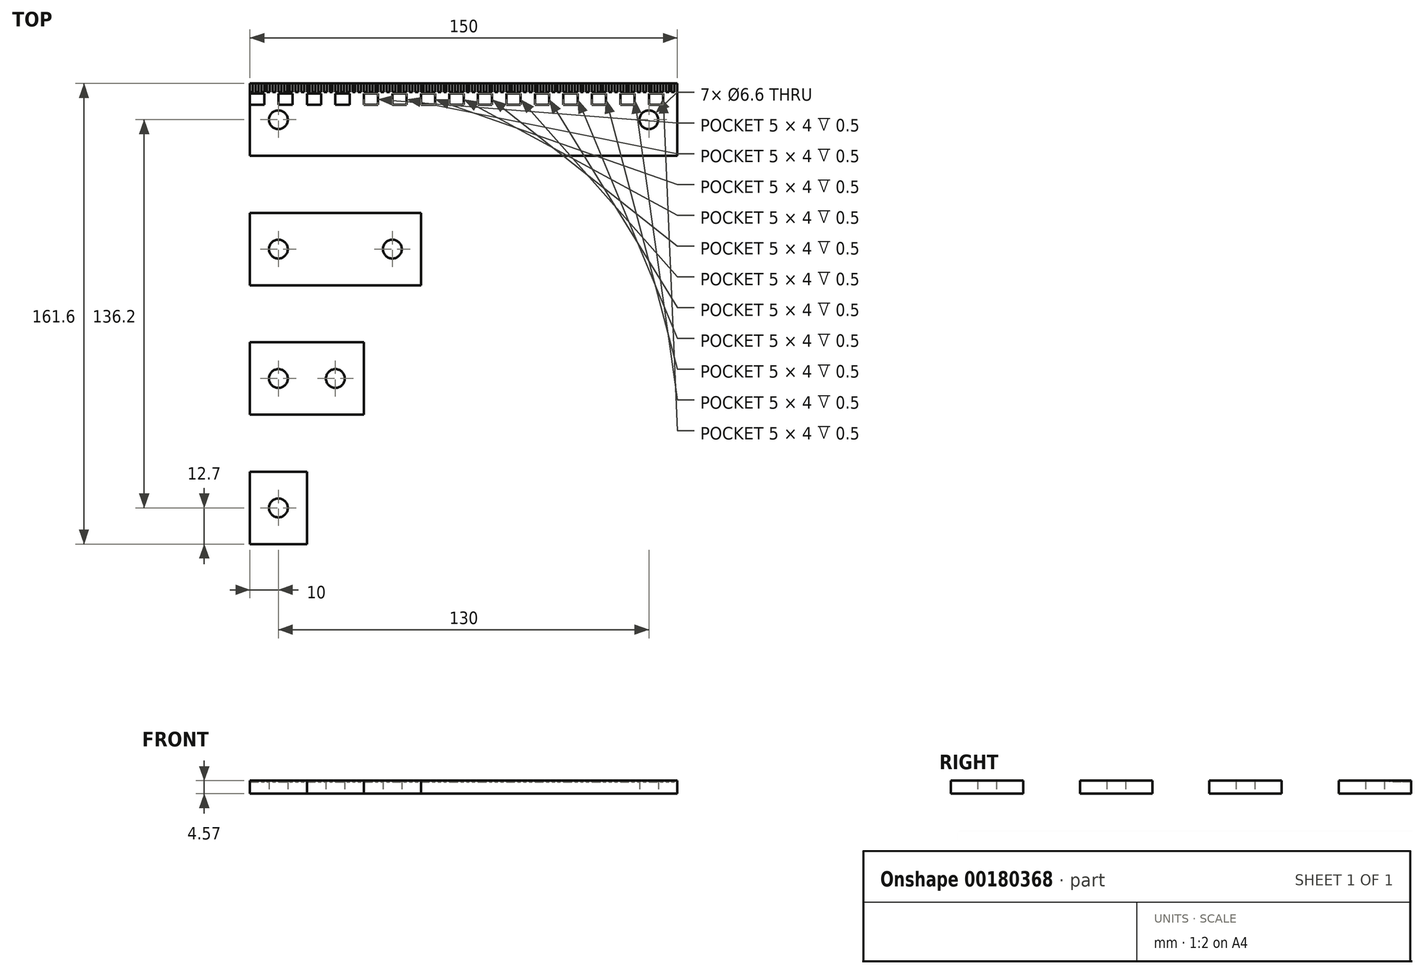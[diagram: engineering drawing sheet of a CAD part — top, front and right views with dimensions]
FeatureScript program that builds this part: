
annotation { "Feature Type Name" : "Feature", "Feature Type Description" : "" }
export const myFeature = defineFeature(function(context is Context, id is Id, definition is map)
    precondition{}
    {
        {
            var Q0;
            Q0=qCreatedBy(makeId("Top.planeOp"),FACE);
            var sketch = newSketch(context, id + "F0", { "sketchPlane" : qUnion([Q0])});
            skLineSegment(sketch, "E0.bottom", {"start": v(0, 161.6) * mm, "end": v(150, 161.6) * mm});
            skLineSegment(sketch, "E0.top", {"start": v(0, 136.2) * mm, "end": v(150, 136.2) * mm});
            skLineSegment(sketch, "E0.left", {"start": v(0, 161.6) * mm, "end": v(0, 136.2) * mm});
            skLineSegment(sketch, "E0.right", {"start": v(150, 161.6) * mm, "end": v(150, 136.2) * mm});
            skLineSegment(sketch, "E1.bottom", {"start": v(0, 116.2) * mm, "end": v(60, 116.2) * mm});
            skLineSegment(sketch, "E1.top", {"start": v(0, 90.8) * mm, "end": v(60, 90.8) * mm});
            skLineSegment(sketch, "E1.left", {"start": v(0, 116.2) * mm, "end": v(0, 90.8) * mm});
            skLineSegment(sketch, "E1.right", {"start": v(60, 116.2) * mm, "end": v(60, 90.8) * mm});
            skLineSegment(sketch, "E2.bottom", {"start": v(0, 70.8) * mm, "end": v(40, 70.8) * mm});
            skLineSegment(sketch, "E2.top", {"start": v(0, 45.4) * mm, "end": v(40, 45.4) * mm});
            skLineSegment(sketch, "E2.left", {"start": v(0, 70.8) * mm, "end": v(0, 45.4) * mm});
            skLineSegment(sketch, "E2.right", {"start": v(40, 70.8) * mm, "end": v(40, 45.4) * mm});
            skLineSegment(sketch, "E3.bottom", {"start": v(0, 25.4) * mm, "end": v(20, 25.4) * mm});
            skLineSegment(sketch, "E3.top", {"start": v(0, 0) * mm, "end": v(20, 0) * mm});
            skLineSegment(sketch, "E3.left", {"start": v(0, 25.4) * mm, "end": v(0, 0) * mm});
            skLineSegment(sketch, "E3.right", {"start": v(20, 25.4) * mm, "end": v(20, 0) * mm});
            skLineSegment(sketch, "E4", {"start": v(0, 136.2) * mm, "end": v(0, 116.2) * mm, "construction": true});
            skLineSegment(sketch, "E5", {"start": v(0, 90.8) * mm, "end": v(0, 70.8) * mm, "construction": true});
            skLineSegment(sketch, "E6", {"start": v(0, 45.4) * mm, "end": v(0, 25.4) * mm, "construction": true});
            skLineSegment(sketch, "E7", {"start": v(0, 12.7) * mm, "end": v(20, 12.7) * mm, "construction": true});
            skLineSegment(sketch, "E8", {"start": v(0, 58.1) * mm, "end": v(40, 58.1) * mm, "construction": true});
            skLineSegment(sketch, "E9", {"start": v(0, 103.5) * mm, "end": v(60, 103.5) * mm, "construction": true});
            skLineSegment(sketch, "E10", {"start": v(0, 148.9) * mm, "end": v(150, 148.9) * mm, "construction": true});
            skCircle(sketch, "E11", {"center": v(10, 12.7) * mm, "radius": 3.3 * mm});
            skCircle(sketch, "E12", {"center": v(30, 58.1) * mm, "radius": 3.3 * mm});
            skCircle(sketch, "E13", {"center": v(10, 58.1) * mm, "radius": 3.3 * mm});
            skCircle(sketch, "E14", {"center": v(50, 103.5) * mm, "radius": 3.3 * mm});
            skCircle(sketch, "E15", {"center": v(10, 103.5) * mm, "radius": 3.3 * mm});
            skCircle(sketch, "E16", {"center": v(140, 148.9) * mm, "radius": 3.3 * mm});
            skCircle(sketch, "E17", {"center": v(10, 148.9) * mm, "radius": 3.3 * mm});
            skLineSegment(sketch, "E18", {"start": v(10, 148.9) * mm, "end": v(10, 103.5) * mm, "construction": true});
            skLineSegment(sketch, "E19", {"start": v(10, 58.1) * mm, "end": v(10, 103.5) * mm, "construction": true});
            skSolve(sketch);
        }
        {
            var Q0;
            Q0 = qSketchRegion(id + "F0", true);
            extrude(context, id + "F1", {"entities" : qUnion([Q0]), "depth" : 4.57 * mm});
        }
        {
            var Q0;
            Q0=makeQuery(id+"F1.opExtrude","CAP_FACE",FACE,{"disambiguationData":[OSD([sQuery(id+"F0.wireOp",EDGE,"E0.bottom"),sQuery(id+"F0.wireOp",EDGE,"E0.top"),sQuery(id+"F0.wireOp",EDGE,"E0.left"),sQuery(id+"F0.wireOp",EDGE,"E0.right"),sQuery(id+"F0.wireOp",EDGE,"E16"),sQuery(id+"F0.wireOp",EDGE,"E17")])],"isStart":false});
            var sketch = newSketch(context, id + "F2", { "sketchPlane" : qUnion([Q0])});
            skLineSegment(sketch, "E20.bottom", {"start": v(0, 161.6) * mm, "end": v(1, 161.6) * mm});
            skLineSegment(sketch, "E20.top", {"start": v(0, 158.6) * mm, "end": v(1, 158.6) * mm});
            skLineSegment(sketch, "E20.left", {"start": v(0, 161.6) * mm, "end": v(0, 158.6) * mm});
            skLineSegment(sketch, "E20.right", {"start": v(1, 161.6) * mm, "end": v(1, 158.6) * mm});
            skLineSegment(sketch, "E21.1.0.0", {"start": v(3, 161.6) * mm, "end": v(3, 158.6) * mm});
            skLineSegment(sketch, "E21.1.0.1", {"start": v(2, 161.6) * mm, "end": v(2, 158.6) * mm});
            skLineSegment(sketch, "E21.1.0.2", {"start": v(2, 158.6) * mm, "end": v(3, 158.6) * mm});
            skLineSegment(sketch, "E21.1.0.3", {"start": v(2, 161.6) * mm, "end": v(3, 161.6) * mm});
            skLineSegment(sketch, "E21.2.0.0", {"start": v(5, 161.6) * mm, "end": v(5, 158.6) * mm});
            skLineSegment(sketch, "E21.2.0.1", {"start": v(4, 161.6) * mm, "end": v(4, 158.6) * mm});
            skLineSegment(sketch, "E21.2.0.2", {"start": v(4, 158.6) * mm, "end": v(5, 158.6) * mm});
            skLineSegment(sketch, "E21.2.0.3", {"start": v(4, 161.6) * mm, "end": v(5, 161.6) * mm});
            skLineSegment(sketch, "E21.3.0.0", {"start": v(7, 161.6) * mm, "end": v(7, 158.6) * mm});
            skLineSegment(sketch, "E21.3.0.1", {"start": v(6, 161.6) * mm, "end": v(6, 158.6) * mm});
            skLineSegment(sketch, "E21.3.0.2", {"start": v(6, 158.6) * mm, "end": v(7, 158.6) * mm});
            skLineSegment(sketch, "E21.3.0.3", {"start": v(6, 161.6) * mm, "end": v(7, 161.6) * mm});
            skLineSegment(sketch, "E21.4.0.0", {"start": v(9, 161.6) * mm, "end": v(9, 158.6) * mm});
            skLineSegment(sketch, "E21.4.0.1", {"start": v(8, 161.6) * mm, "end": v(8, 158.6) * mm});
            skLineSegment(sketch, "E21.4.0.2", {"start": v(8, 158.6) * mm, "end": v(9, 158.6) * mm});
            skLineSegment(sketch, "E21.4.0.3", {"start": v(8, 161.6) * mm, "end": v(9, 161.6) * mm});
            skLineSegment(sketch, "E21.5.0.0", {"start": v(11, 161.6) * mm, "end": v(11, 158.6) * mm});
            skLineSegment(sketch, "E21.5.0.1", {"start": v(10, 161.6) * mm, "end": v(10, 158.6) * mm});
            skLineSegment(sketch, "E21.5.0.2", {"start": v(10, 158.6) * mm, "end": v(11, 158.6) * mm});
            skLineSegment(sketch, "E21.5.0.3", {"start": v(10, 161.6) * mm, "end": v(11, 161.6) * mm});
            skLineSegment(sketch, "E21.6.0.0", {"start": v(13, 161.6) * mm, "end": v(13, 158.6) * mm});
            skLineSegment(sketch, "E21.6.0.1", {"start": v(12, 161.6) * mm, "end": v(12, 158.6) * mm});
            skLineSegment(sketch, "E21.6.0.2", {"start": v(12, 158.6) * mm, "end": v(13, 158.6) * mm});
            skLineSegment(sketch, "E21.6.0.3", {"start": v(12, 161.6) * mm, "end": v(13, 161.6) * mm});
            skLineSegment(sketch, "E21.7.0.0", {"start": v(15, 161.6) * mm, "end": v(15, 158.6) * mm});
            skLineSegment(sketch, "E21.7.0.1", {"start": v(14, 161.6) * mm, "end": v(14, 158.6) * mm});
            skLineSegment(sketch, "E21.7.0.2", {"start": v(14, 158.6) * mm, "end": v(15, 158.6) * mm});
            skLineSegment(sketch, "E21.7.0.3", {"start": v(14, 161.6) * mm, "end": v(15, 161.6) * mm});
            skLineSegment(sketch, "E21.8.0.0", {"start": v(17, 161.6) * mm, "end": v(17, 158.6) * mm});
            skLineSegment(sketch, "E21.8.0.1", {"start": v(16, 161.6) * mm, "end": v(16, 158.6) * mm});
            skLineSegment(sketch, "E21.8.0.2", {"start": v(16, 158.6) * mm, "end": v(17, 158.6) * mm});
            skLineSegment(sketch, "E21.8.0.3", {"start": v(16, 161.6) * mm, "end": v(17, 161.6) * mm});
            skLineSegment(sketch, "E21.9.0.0", {"start": v(19, 161.6) * mm, "end": v(19, 158.6) * mm});
            skLineSegment(sketch, "E21.9.0.1", {"start": v(18, 161.6) * mm, "end": v(18, 158.6) * mm});
            skLineSegment(sketch, "E21.9.0.2", {"start": v(18, 158.6) * mm, "end": v(19, 158.6) * mm});
            skLineSegment(sketch, "E21.9.0.3", {"start": v(18, 161.6) * mm, "end": v(19, 161.6) * mm});
            skLineSegment(sketch, "E21.10.0.0", {"start": v(21, 161.6) * mm, "end": v(21, 158.6) * mm});
            skLineSegment(sketch, "E21.10.0.1", {"start": v(20, 161.6) * mm, "end": v(20, 158.6) * mm});
            skLineSegment(sketch, "E21.10.0.2", {"start": v(20, 158.6) * mm, "end": v(21, 158.6) * mm});
            skLineSegment(sketch, "E21.10.0.3", {"start": v(20, 161.6) * mm, "end": v(21, 161.6) * mm});
            skLineSegment(sketch, "E21.11.0.0", {"start": v(23, 161.6) * mm, "end": v(23, 158.6) * mm});
            skLineSegment(sketch, "E21.11.0.1", {"start": v(22, 161.6) * mm, "end": v(22, 158.6) * mm});
            skLineSegment(sketch, "E21.11.0.2", {"start": v(22, 158.6) * mm, "end": v(23, 158.6) * mm});
            skLineSegment(sketch, "E21.11.0.3", {"start": v(22, 161.6) * mm, "end": v(23, 161.6) * mm});
            skLineSegment(sketch, "E21.12.0.0", {"start": v(25, 161.6) * mm, "end": v(25, 158.6) * mm});
            skLineSegment(sketch, "E21.12.0.1", {"start": v(24, 161.6) * mm, "end": v(24, 158.6) * mm});
            skLineSegment(sketch, "E21.12.0.2", {"start": v(24, 158.6) * mm, "end": v(25, 158.6) * mm});
            skLineSegment(sketch, "E21.12.0.3", {"start": v(24, 161.6) * mm, "end": v(25, 161.6) * mm});
            skLineSegment(sketch, "E21.13.0.0", {"start": v(27, 161.6) * mm, "end": v(27, 158.6) * mm});
            skLineSegment(sketch, "E21.13.0.1", {"start": v(26, 161.6) * mm, "end": v(26, 158.6) * mm});
            skLineSegment(sketch, "E21.13.0.2", {"start": v(26, 158.6) * mm, "end": v(27, 158.6) * mm});
            skLineSegment(sketch, "E21.13.0.3", {"start": v(26, 161.6) * mm, "end": v(27, 161.6) * mm});
            skLineSegment(sketch, "E21.14.0.0", {"start": v(29, 161.6) * mm, "end": v(29, 158.6) * mm});
            skLineSegment(sketch, "E21.14.0.1", {"start": v(28, 161.6) * mm, "end": v(28, 158.6) * mm});
            skLineSegment(sketch, "E21.14.0.2", {"start": v(28, 158.6) * mm, "end": v(29, 158.6) * mm});
            skLineSegment(sketch, "E21.14.0.3", {"start": v(28, 161.6) * mm, "end": v(29, 161.6) * mm});
            skLineSegment(sketch, "E21.15.0.0", {"start": v(31, 161.6) * mm, "end": v(31, 158.6) * mm});
            skLineSegment(sketch, "E21.15.0.1", {"start": v(30, 161.6) * mm, "end": v(30, 158.6) * mm});
            skLineSegment(sketch, "E21.15.0.2", {"start": v(30, 158.6) * mm, "end": v(31, 158.6) * mm});
            skLineSegment(sketch, "E21.15.0.3", {"start": v(30, 161.6) * mm, "end": v(31, 161.6) * mm});
            skLineSegment(sketch, "E21.16.0.0", {"start": v(33, 161.6) * mm, "end": v(33, 158.6) * mm});
            skLineSegment(sketch, "E21.16.0.1", {"start": v(32, 161.6) * mm, "end": v(32, 158.6) * mm});
            skLineSegment(sketch, "E21.16.0.2", {"start": v(32, 158.6) * mm, "end": v(33, 158.6) * mm});
            skLineSegment(sketch, "E21.16.0.3", {"start": v(32, 161.6) * mm, "end": v(33, 161.6) * mm});
            skLineSegment(sketch, "E21.17.0.0", {"start": v(35, 161.6) * mm, "end": v(35, 158.6) * mm});
            skLineSegment(sketch, "E21.17.0.1", {"start": v(34, 161.6) * mm, "end": v(34, 158.6) * mm});
            skLineSegment(sketch, "E21.17.0.2", {"start": v(34, 158.6) * mm, "end": v(35, 158.6) * mm});
            skLineSegment(sketch, "E21.17.0.3", {"start": v(34, 161.6) * mm, "end": v(35, 161.6) * mm});
            skLineSegment(sketch, "E21.18.0.0", {"start": v(37, 161.6) * mm, "end": v(37, 158.6) * mm});
            skLineSegment(sketch, "E21.18.0.1", {"start": v(36, 161.6) * mm, "end": v(36, 158.6) * mm});
            skLineSegment(sketch, "E21.18.0.2", {"start": v(36, 158.6) * mm, "end": v(37, 158.6) * mm});
            skLineSegment(sketch, "E21.18.0.3", {"start": v(36, 161.6) * mm, "end": v(37, 161.6) * mm});
            skLineSegment(sketch, "E21.19.0.0", {"start": v(39, 161.6) * mm, "end": v(39, 158.6) * mm});
            skLineSegment(sketch, "E21.19.0.1", {"start": v(38, 161.6) * mm, "end": v(38, 158.6) * mm});
            skLineSegment(sketch, "E21.19.0.2", {"start": v(38, 158.6) * mm, "end": v(39, 158.6) * mm});
            skLineSegment(sketch, "E21.19.0.3", {"start": v(38, 161.6) * mm, "end": v(39, 161.6) * mm});
            skLineSegment(sketch, "E21.20.0.0", {"start": v(41, 161.6) * mm, "end": v(41, 158.6) * mm});
            skLineSegment(sketch, "E21.20.0.1", {"start": v(40, 161.6) * mm, "end": v(40, 158.6) * mm});
            skLineSegment(sketch, "E21.20.0.2", {"start": v(40, 158.6) * mm, "end": v(41, 158.6) * mm});
            skLineSegment(sketch, "E21.20.0.3", {"start": v(40, 161.6) * mm, "end": v(41, 161.6) * mm});
            skLineSegment(sketch, "E21.21.0.0", {"start": v(43, 161.6) * mm, "end": v(43, 158.6) * mm});
            skLineSegment(sketch, "E21.21.0.1", {"start": v(42, 161.6) * mm, "end": v(42, 158.6) * mm});
            skLineSegment(sketch, "E21.21.0.2", {"start": v(42, 158.6) * mm, "end": v(43, 158.6) * mm});
            skLineSegment(sketch, "E21.21.0.3", {"start": v(42, 161.6) * mm, "end": v(43, 161.6) * mm});
            skLineSegment(sketch, "E21.22.0.0", {"start": v(45, 161.6) * mm, "end": v(45, 158.6) * mm});
            skLineSegment(sketch, "E21.22.0.1", {"start": v(44, 161.6) * mm, "end": v(44, 158.6) * mm});
            skLineSegment(sketch, "E21.22.0.2", {"start": v(44, 158.6) * mm, "end": v(45, 158.6) * mm});
            skLineSegment(sketch, "E21.22.0.3", {"start": v(44, 161.6) * mm, "end": v(45, 161.6) * mm});
            skLineSegment(sketch, "E21.23.0.0", {"start": v(47, 161.6) * mm, "end": v(47, 158.6) * mm});
            skLineSegment(sketch, "E21.23.0.1", {"start": v(46, 161.6) * mm, "end": v(46, 158.6) * mm});
            skLineSegment(sketch, "E21.23.0.2", {"start": v(46, 158.6) * mm, "end": v(47, 158.6) * mm});
            skLineSegment(sketch, "E21.23.0.3", {"start": v(46, 161.6) * mm, "end": v(47, 161.6) * mm});
            skLineSegment(sketch, "E21.24.0.0", {"start": v(49, 161.6) * mm, "end": v(49, 158.6) * mm});
            skLineSegment(sketch, "E21.24.0.1", {"start": v(48, 161.6) * mm, "end": v(48, 158.6) * mm});
            skLineSegment(sketch, "E21.24.0.2", {"start": v(48, 158.6) * mm, "end": v(49, 158.6) * mm});
            skLineSegment(sketch, "E21.24.0.3", {"start": v(48, 161.6) * mm, "end": v(49, 161.6) * mm});
            skLineSegment(sketch, "E21.25.0.0", {"start": v(51, 161.6) * mm, "end": v(51, 158.6) * mm});
            skLineSegment(sketch, "E21.25.0.1", {"start": v(50, 161.6) * mm, "end": v(50, 158.6) * mm});
            skLineSegment(sketch, "E21.25.0.2", {"start": v(50, 158.6) * mm, "end": v(51, 158.6) * mm});
            skLineSegment(sketch, "E21.25.0.3", {"start": v(50, 161.6) * mm, "end": v(51, 161.6) * mm});
            skLineSegment(sketch, "E21.26.0.0", {"start": v(53, 161.6) * mm, "end": v(53, 158.6) * mm});
            skLineSegment(sketch, "E21.26.0.1", {"start": v(52, 161.6) * mm, "end": v(52, 158.6) * mm});
            skLineSegment(sketch, "E21.26.0.2", {"start": v(52, 158.6) * mm, "end": v(53, 158.6) * mm});
            skLineSegment(sketch, "E21.26.0.3", {"start": v(52, 161.6) * mm, "end": v(53, 161.6) * mm});
            skLineSegment(sketch, "E21.27.0.0", {"start": v(55, 161.6) * mm, "end": v(55, 158.6) * mm});
            skLineSegment(sketch, "E21.27.0.1", {"start": v(54, 161.6) * mm, "end": v(54, 158.6) * mm});
            skLineSegment(sketch, "E21.27.0.2", {"start": v(54, 158.6) * mm, "end": v(55, 158.6) * mm});
            skLineSegment(sketch, "E21.27.0.3", {"start": v(54, 161.6) * mm, "end": v(55, 161.6) * mm});
            skLineSegment(sketch, "E21.28.0.0", {"start": v(57, 161.6) * mm, "end": v(57, 158.6) * mm});
            skLineSegment(sketch, "E21.28.0.1", {"start": v(56, 161.6) * mm, "end": v(56, 158.6) * mm});
            skLineSegment(sketch, "E21.28.0.2", {"start": v(56, 158.6) * mm, "end": v(57, 158.6) * mm});
            skLineSegment(sketch, "E21.28.0.3", {"start": v(56, 161.6) * mm, "end": v(57, 161.6) * mm});
            skLineSegment(sketch, "E21.29.0.0", {"start": v(59, 161.6) * mm, "end": v(59, 158.6) * mm});
            skLineSegment(sketch, "E21.29.0.1", {"start": v(58, 161.6) * mm, "end": v(58, 158.6) * mm});
            skLineSegment(sketch, "E21.29.0.2", {"start": v(58, 158.6) * mm, "end": v(59, 158.6) * mm});
            skLineSegment(sketch, "E21.29.0.3", {"start": v(58, 161.6) * mm, "end": v(59, 161.6) * mm});
            skLineSegment(sketch, "E21.30.0.0", {"start": v(61, 161.6) * mm, "end": v(61, 158.6) * mm});
            skLineSegment(sketch, "E21.30.0.1", {"start": v(60, 161.6) * mm, "end": v(60, 158.6) * mm});
            skLineSegment(sketch, "E21.30.0.2", {"start": v(60, 158.6) * mm, "end": v(61, 158.6) * mm});
            skLineSegment(sketch, "E21.30.0.3", {"start": v(60, 161.6) * mm, "end": v(61, 161.6) * mm});
            skLineSegment(sketch, "E21.31.0.0", {"start": v(63, 161.6) * mm, "end": v(63, 158.6) * mm});
            skLineSegment(sketch, "E21.31.0.1", {"start": v(62, 161.6) * mm, "end": v(62, 158.6) * mm});
            skLineSegment(sketch, "E21.31.0.2", {"start": v(62, 158.6) * mm, "end": v(63, 158.6) * mm});
            skLineSegment(sketch, "E21.31.0.3", {"start": v(62, 161.6) * mm, "end": v(63, 161.6) * mm});
            skLineSegment(sketch, "E21.32.0.0", {"start": v(65, 161.6) * mm, "end": v(65, 158.6) * mm});
            skLineSegment(sketch, "E21.32.0.1", {"start": v(64, 161.6) * mm, "end": v(64, 158.6) * mm});
            skLineSegment(sketch, "E21.32.0.2", {"start": v(64, 158.6) * mm, "end": v(65, 158.6) * mm});
            skLineSegment(sketch, "E21.32.0.3", {"start": v(64, 161.6) * mm, "end": v(65, 161.6) * mm});
            skLineSegment(sketch, "E21.33.0.0", {"start": v(67, 161.6) * mm, "end": v(67, 158.6) * mm});
            skLineSegment(sketch, "E21.33.0.1", {"start": v(66, 161.6) * mm, "end": v(66, 158.6) * mm});
            skLineSegment(sketch, "E21.33.0.2", {"start": v(66, 158.6) * mm, "end": v(67, 158.6) * mm});
            skLineSegment(sketch, "E21.33.0.3", {"start": v(66, 161.6) * mm, "end": v(67, 161.6) * mm});
            skLineSegment(sketch, "E21.34.0.0", {"start": v(69, 161.6) * mm, "end": v(69, 158.6) * mm});
            skLineSegment(sketch, "E21.34.0.1", {"start": v(68, 161.6) * mm, "end": v(68, 158.6) * mm});
            skLineSegment(sketch, "E21.34.0.2", {"start": v(68, 158.6) * mm, "end": v(69, 158.6) * mm});
            skLineSegment(sketch, "E21.34.0.3", {"start": v(68, 161.6) * mm, "end": v(69, 161.6) * mm});
            skLineSegment(sketch, "E21.35.0.0", {"start": v(71, 161.6) * mm, "end": v(71, 158.6) * mm});
            skLineSegment(sketch, "E21.35.0.1", {"start": v(70, 161.6) * mm, "end": v(70, 158.6) * mm});
            skLineSegment(sketch, "E21.35.0.2", {"start": v(70, 158.6) * mm, "end": v(71, 158.6) * mm});
            skLineSegment(sketch, "E21.35.0.3", {"start": v(70, 161.6) * mm, "end": v(71, 161.6) * mm});
            skLineSegment(sketch, "E21.36.0.0", {"start": v(73, 161.6) * mm, "end": v(73, 158.6) * mm});
            skLineSegment(sketch, "E21.36.0.1", {"start": v(72, 161.6) * mm, "end": v(72, 158.6) * mm});
            skLineSegment(sketch, "E21.36.0.2", {"start": v(72, 158.6) * mm, "end": v(73, 158.6) * mm});
            skLineSegment(sketch, "E21.36.0.3", {"start": v(72, 161.6) * mm, "end": v(73, 161.6) * mm});
            skLineSegment(sketch, "E21.37.0.0", {"start": v(75, 161.6) * mm, "end": v(75, 158.6) * mm});
            skLineSegment(sketch, "E21.37.0.1", {"start": v(74, 161.6) * mm, "end": v(74, 158.6) * mm});
            skLineSegment(sketch, "E21.37.0.2", {"start": v(74, 158.6) * mm, "end": v(75, 158.6) * mm});
            skLineSegment(sketch, "E21.37.0.3", {"start": v(74, 161.6) * mm, "end": v(75, 161.6) * mm});
            skLineSegment(sketch, "E21.38.0.0", {"start": v(77, 161.6) * mm, "end": v(77, 158.6) * mm});
            skLineSegment(sketch, "E21.38.0.1", {"start": v(76, 161.6) * mm, "end": v(76, 158.6) * mm});
            skLineSegment(sketch, "E21.38.0.2", {"start": v(76, 158.6) * mm, "end": v(77, 158.6) * mm});
            skLineSegment(sketch, "E21.38.0.3", {"start": v(76, 161.6) * mm, "end": v(77, 161.6) * mm});
            skLineSegment(sketch, "E21.39.0.0", {"start": v(79, 161.6) * mm, "end": v(79, 158.6) * mm});
            skLineSegment(sketch, "E21.39.0.1", {"start": v(78, 161.6) * mm, "end": v(78, 158.6) * mm});
            skLineSegment(sketch, "E21.39.0.2", {"start": v(78, 158.6) * mm, "end": v(79, 158.6) * mm});
            skLineSegment(sketch, "E21.39.0.3", {"start": v(78, 161.6) * mm, "end": v(79, 161.6) * mm});
            skLineSegment(sketch, "E21.40.0.0", {"start": v(81, 161.6) * mm, "end": v(81, 158.6) * mm});
            skLineSegment(sketch, "E21.40.0.1", {"start": v(80, 161.6) * mm, "end": v(80, 158.6) * mm});
            skLineSegment(sketch, "E21.40.0.2", {"start": v(80, 158.6) * mm, "end": v(81, 158.6) * mm});
            skLineSegment(sketch, "E21.40.0.3", {"start": v(80, 161.6) * mm, "end": v(81, 161.6) * mm});
            skLineSegment(sketch, "E21.41.0.0", {"start": v(83, 161.6) * mm, "end": v(83, 158.6) * mm});
            skLineSegment(sketch, "E21.41.0.1", {"start": v(82, 161.6) * mm, "end": v(82, 158.6) * mm});
            skLineSegment(sketch, "E21.41.0.2", {"start": v(82, 158.6) * mm, "end": v(83, 158.6) * mm});
            skLineSegment(sketch, "E21.41.0.3", {"start": v(82, 161.6) * mm, "end": v(83, 161.6) * mm});
            skLineSegment(sketch, "E21.42.0.0", {"start": v(85, 161.6) * mm, "end": v(85, 158.6) * mm});
            skLineSegment(sketch, "E21.42.0.1", {"start": v(84, 161.6) * mm, "end": v(84, 158.6) * mm});
            skLineSegment(sketch, "E21.42.0.2", {"start": v(84, 158.6) * mm, "end": v(85, 158.6) * mm});
            skLineSegment(sketch, "E21.42.0.3", {"start": v(84, 161.6) * mm, "end": v(85, 161.6) * mm});
            skLineSegment(sketch, "E21.43.0.0", {"start": v(87, 161.6) * mm, "end": v(87, 158.6) * mm});
            skLineSegment(sketch, "E21.43.0.1", {"start": v(86, 161.6) * mm, "end": v(86, 158.6) * mm});
            skLineSegment(sketch, "E21.43.0.2", {"start": v(86, 158.6) * mm, "end": v(87, 158.6) * mm});
            skLineSegment(sketch, "E21.43.0.3", {"start": v(86, 161.6) * mm, "end": v(87, 161.6) * mm});
            skLineSegment(sketch, "E21.44.0.0", {"start": v(89, 161.6) * mm, "end": v(89, 158.6) * mm});
            skLineSegment(sketch, "E21.44.0.1", {"start": v(88, 161.6) * mm, "end": v(88, 158.6) * mm});
            skLineSegment(sketch, "E21.44.0.2", {"start": v(88, 158.6) * mm, "end": v(89, 158.6) * mm});
            skLineSegment(sketch, "E21.44.0.3", {"start": v(88, 161.6) * mm, "end": v(89, 161.6) * mm});
            skLineSegment(sketch, "E21.45.0.0", {"start": v(91, 161.6) * mm, "end": v(91, 158.6) * mm});
            skLineSegment(sketch, "E21.45.0.1", {"start": v(90, 161.6) * mm, "end": v(90, 158.6) * mm});
            skLineSegment(sketch, "E21.45.0.2", {"start": v(90, 158.6) * mm, "end": v(91, 158.6) * mm});
            skLineSegment(sketch, "E21.45.0.3", {"start": v(90, 161.6) * mm, "end": v(91, 161.6) * mm});
            skLineSegment(sketch, "E21.46.0.0", {"start": v(93, 161.6) * mm, "end": v(93, 158.6) * mm});
            skLineSegment(sketch, "E21.46.0.1", {"start": v(92, 161.6) * mm, "end": v(92, 158.6) * mm});
            skLineSegment(sketch, "E21.46.0.2", {"start": v(92, 158.6) * mm, "end": v(93, 158.6) * mm});
            skLineSegment(sketch, "E21.46.0.3", {"start": v(92, 161.6) * mm, "end": v(93, 161.6) * mm});
            skLineSegment(sketch, "E21.47.0.0", {"start": v(95, 161.6) * mm, "end": v(95, 158.6) * mm});
            skLineSegment(sketch, "E21.47.0.1", {"start": v(94, 161.6) * mm, "end": v(94, 158.6) * mm});
            skLineSegment(sketch, "E21.47.0.2", {"start": v(94, 158.6) * mm, "end": v(95, 158.6) * mm});
            skLineSegment(sketch, "E21.47.0.3", {"start": v(94, 161.6) * mm, "end": v(95, 161.6) * mm});
            skLineSegment(sketch, "E21.48.0.0", {"start": v(97, 161.6) * mm, "end": v(97, 158.6) * mm});
            skLineSegment(sketch, "E21.48.0.1", {"start": v(96, 161.6) * mm, "end": v(96, 158.6) * mm});
            skLineSegment(sketch, "E21.48.0.2", {"start": v(96, 158.6) * mm, "end": v(97, 158.6) * mm});
            skLineSegment(sketch, "E21.48.0.3", {"start": v(96, 161.6) * mm, "end": v(97, 161.6) * mm});
            skLineSegment(sketch, "E21.49.0.0", {"start": v(99, 161.6) * mm, "end": v(99, 158.6) * mm});
            skLineSegment(sketch, "E21.49.0.1", {"start": v(98, 161.6) * mm, "end": v(98, 158.6) * mm});
            skLineSegment(sketch, "E21.49.0.2", {"start": v(98, 158.6) * mm, "end": v(99, 158.6) * mm});
            skLineSegment(sketch, "E21.49.0.3", {"start": v(98, 161.6) * mm, "end": v(99, 161.6) * mm});
            skLineSegment(sketch, "E21.50.0.0", {"start": v(101, 161.6) * mm, "end": v(101, 158.6) * mm});
            skLineSegment(sketch, "E21.50.0.1", {"start": v(100, 161.6) * mm, "end": v(100, 158.6) * mm});
            skLineSegment(sketch, "E21.50.0.2", {"start": v(100, 158.6) * mm, "end": v(101, 158.6) * mm});
            skLineSegment(sketch, "E21.50.0.3", {"start": v(100, 161.6) * mm, "end": v(101, 161.6) * mm});
            skLineSegment(sketch, "E21.51.0.0", {"start": v(103, 161.6) * mm, "end": v(103, 158.6) * mm});
            skLineSegment(sketch, "E21.51.0.1", {"start": v(102, 161.6) * mm, "end": v(102, 158.6) * mm});
            skLineSegment(sketch, "E21.51.0.2", {"start": v(102, 158.6) * mm, "end": v(103, 158.6) * mm});
            skLineSegment(sketch, "E21.51.0.3", {"start": v(102, 161.6) * mm, "end": v(103, 161.6) * mm});
            skLineSegment(sketch, "E21.52.0.0", {"start": v(105, 161.6) * mm, "end": v(105, 158.6) * mm});
            skLineSegment(sketch, "E21.52.0.1", {"start": v(104, 161.6) * mm, "end": v(104, 158.6) * mm});
            skLineSegment(sketch, "E21.52.0.2", {"start": v(104, 158.6) * mm, "end": v(105, 158.6) * mm});
            skLineSegment(sketch, "E21.52.0.3", {"start": v(104, 161.6) * mm, "end": v(105, 161.6) * mm});
            skLineSegment(sketch, "E21.53.0.0", {"start": v(107, 161.6) * mm, "end": v(107, 158.6) * mm});
            skLineSegment(sketch, "E21.53.0.1", {"start": v(106, 161.6) * mm, "end": v(106, 158.6) * mm});
            skLineSegment(sketch, "E21.53.0.2", {"start": v(106, 158.6) * mm, "end": v(107, 158.6) * mm});
            skLineSegment(sketch, "E21.53.0.3", {"start": v(106, 161.6) * mm, "end": v(107, 161.6) * mm});
            skLineSegment(sketch, "E21.54.0.0", {"start": v(109, 161.6) * mm, "end": v(109, 158.6) * mm});
            skLineSegment(sketch, "E21.54.0.1", {"start": v(108, 161.6) * mm, "end": v(108, 158.6) * mm});
            skLineSegment(sketch, "E21.54.0.2", {"start": v(108, 158.6) * mm, "end": v(109, 158.6) * mm});
            skLineSegment(sketch, "E21.54.0.3", {"start": v(108, 161.6) * mm, "end": v(109, 161.6) * mm});
            skLineSegment(sketch, "E21.55.0.0", {"start": v(111, 161.6) * mm, "end": v(111, 158.6) * mm});
            skLineSegment(sketch, "E21.55.0.1", {"start": v(110, 161.6) * mm, "end": v(110, 158.6) * mm});
            skLineSegment(sketch, "E21.55.0.2", {"start": v(110, 158.6) * mm, "end": v(111, 158.6) * mm});
            skLineSegment(sketch, "E21.55.0.3", {"start": v(110, 161.6) * mm, "end": v(111, 161.6) * mm});
            skLineSegment(sketch, "E21.56.0.0", {"start": v(113, 161.6) * mm, "end": v(113, 158.6) * mm});
            skLineSegment(sketch, "E21.56.0.1", {"start": v(112, 161.6) * mm, "end": v(112, 158.6) * mm});
            skLineSegment(sketch, "E21.56.0.2", {"start": v(112, 158.6) * mm, "end": v(113, 158.6) * mm});
            skLineSegment(sketch, "E21.56.0.3", {"start": v(112, 161.6) * mm, "end": v(113, 161.6) * mm});
            skLineSegment(sketch, "E21.57.0.0", {"start": v(115, 161.6) * mm, "end": v(115, 158.6) * mm});
            skLineSegment(sketch, "E21.57.0.1", {"start": v(114, 161.6) * mm, "end": v(114, 158.6) * mm});
            skLineSegment(sketch, "E21.57.0.2", {"start": v(114, 158.6) * mm, "end": v(115, 158.6) * mm});
            skLineSegment(sketch, "E21.57.0.3", {"start": v(114, 161.6) * mm, "end": v(115, 161.6) * mm});
            skLineSegment(sketch, "E21.58.0.0", {"start": v(117, 161.6) * mm, "end": v(117, 158.6) * mm});
            skLineSegment(sketch, "E21.58.0.1", {"start": v(116, 161.6) * mm, "end": v(116, 158.6) * mm});
            skLineSegment(sketch, "E21.58.0.2", {"start": v(116, 158.6) * mm, "end": v(117, 158.6) * mm});
            skLineSegment(sketch, "E21.58.0.3", {"start": v(116, 161.6) * mm, "end": v(117, 161.6) * mm});
            skLineSegment(sketch, "E21.59.0.0", {"start": v(119, 161.6) * mm, "end": v(119, 158.6) * mm});
            skLineSegment(sketch, "E21.59.0.1", {"start": v(118, 161.6) * mm, "end": v(118, 158.6) * mm});
            skLineSegment(sketch, "E21.59.0.2", {"start": v(118, 158.6) * mm, "end": v(119, 158.6) * mm});
            skLineSegment(sketch, "E21.59.0.3", {"start": v(118, 161.6) * mm, "end": v(119, 161.6) * mm});
            skLineSegment(sketch, "E21.60.0.0", {"start": v(121, 161.6) * mm, "end": v(121, 158.6) * mm});
            skLineSegment(sketch, "E21.60.0.1", {"start": v(120, 161.6) * mm, "end": v(120, 158.6) * mm});
            skLineSegment(sketch, "E21.60.0.2", {"start": v(120, 158.6) * mm, "end": v(121, 158.6) * mm});
            skLineSegment(sketch, "E21.60.0.3", {"start": v(120, 161.6) * mm, "end": v(121, 161.6) * mm});
            skLineSegment(sketch, "E21.61.0.0", {"start": v(123, 161.6) * mm, "end": v(123, 158.6) * mm});
            skLineSegment(sketch, "E21.61.0.1", {"start": v(122, 161.6) * mm, "end": v(122, 158.6) * mm});
            skLineSegment(sketch, "E21.61.0.2", {"start": v(122, 158.6) * mm, "end": v(123, 158.6) * mm});
            skLineSegment(sketch, "E21.61.0.3", {"start": v(122, 161.6) * mm, "end": v(123, 161.6) * mm});
            skLineSegment(sketch, "E21.62.0.0", {"start": v(125, 161.6) * mm, "end": v(125, 158.6) * mm});
            skLineSegment(sketch, "E21.62.0.1", {"start": v(124, 161.6) * mm, "end": v(124, 158.6) * mm});
            skLineSegment(sketch, "E21.62.0.2", {"start": v(124, 158.6) * mm, "end": v(125, 158.6) * mm});
            skLineSegment(sketch, "E21.62.0.3", {"start": v(124, 161.6) * mm, "end": v(125, 161.6) * mm});
            skLineSegment(sketch, "E21.63.0.0", {"start": v(127, 161.6) * mm, "end": v(127, 158.6) * mm});
            skLineSegment(sketch, "E21.63.0.1", {"start": v(126, 161.6) * mm, "end": v(126, 158.6) * mm});
            skLineSegment(sketch, "E21.63.0.2", {"start": v(126, 158.6) * mm, "end": v(127, 158.6) * mm});
            skLineSegment(sketch, "E21.63.0.3", {"start": v(126, 161.6) * mm, "end": v(127, 161.6) * mm});
            skLineSegment(sketch, "E21.64.0.0", {"start": v(129, 161.6) * mm, "end": v(129, 158.6) * mm});
            skLineSegment(sketch, "E21.64.0.1", {"start": v(128, 161.6) * mm, "end": v(128, 158.6) * mm});
            skLineSegment(sketch, "E21.64.0.2", {"start": v(128, 158.6) * mm, "end": v(129, 158.6) * mm});
            skLineSegment(sketch, "E21.64.0.3", {"start": v(128, 161.6) * mm, "end": v(129, 161.6) * mm});
            skLineSegment(sketch, "E21.65.0.0", {"start": v(131, 161.6) * mm, "end": v(131, 158.6) * mm});
            skLineSegment(sketch, "E21.65.0.1", {"start": v(130, 161.6) * mm, "end": v(130, 158.6) * mm});
            skLineSegment(sketch, "E21.65.0.2", {"start": v(130, 158.6) * mm, "end": v(131, 158.6) * mm});
            skLineSegment(sketch, "E21.65.0.3", {"start": v(130, 161.6) * mm, "end": v(131, 161.6) * mm});
            skLineSegment(sketch, "E21.66.0.0", {"start": v(133, 161.6) * mm, "end": v(133, 158.6) * mm});
            skLineSegment(sketch, "E21.66.0.1", {"start": v(132, 161.6) * mm, "end": v(132, 158.6) * mm});
            skLineSegment(sketch, "E21.66.0.2", {"start": v(132, 158.6) * mm, "end": v(133, 158.6) * mm});
            skLineSegment(sketch, "E21.66.0.3", {"start": v(132, 161.6) * mm, "end": v(133, 161.6) * mm});
            skLineSegment(sketch, "E21.67.0.0", {"start": v(135, 161.6) * mm, "end": v(135, 158.6) * mm});
            skLineSegment(sketch, "E21.67.0.1", {"start": v(134, 161.6) * mm, "end": v(134, 158.6) * mm});
            skLineSegment(sketch, "E21.67.0.2", {"start": v(134, 158.6) * mm, "end": v(135, 158.6) * mm});
            skLineSegment(sketch, "E21.67.0.3", {"start": v(134, 161.6) * mm, "end": v(135, 161.6) * mm});
            skLineSegment(sketch, "E21.68.0.0", {"start": v(137, 161.6) * mm, "end": v(137, 158.6) * mm});
            skLineSegment(sketch, "E21.68.0.1", {"start": v(136, 161.6) * mm, "end": v(136, 158.6) * mm});
            skLineSegment(sketch, "E21.68.0.2", {"start": v(136, 158.6) * mm, "end": v(137, 158.6) * mm});
            skLineSegment(sketch, "E21.68.0.3", {"start": v(136, 161.6) * mm, "end": v(137, 161.6) * mm});
            skLineSegment(sketch, "E21.69.0.0", {"start": v(139, 161.6) * mm, "end": v(139, 158.6) * mm});
            skLineSegment(sketch, "E21.69.0.1", {"start": v(138, 161.6) * mm, "end": v(138, 158.6) * mm});
            skLineSegment(sketch, "E21.69.0.2", {"start": v(138, 158.6) * mm, "end": v(139, 158.6) * mm});
            skLineSegment(sketch, "E21.69.0.3", {"start": v(138, 161.6) * mm, "end": v(139, 161.6) * mm});
            skLineSegment(sketch, "E21.70.0.0", {"start": v(141, 161.6) * mm, "end": v(141, 158.6) * mm});
            skLineSegment(sketch, "E21.70.0.1", {"start": v(140, 161.6) * mm, "end": v(140, 158.6) * mm});
            skLineSegment(sketch, "E21.70.0.2", {"start": v(140, 158.6) * mm, "end": v(141, 158.6) * mm});
            skLineSegment(sketch, "E21.70.0.3", {"start": v(140, 161.6) * mm, "end": v(141, 161.6) * mm});
            skLineSegment(sketch, "E21.71.0.0", {"start": v(143, 161.6) * mm, "end": v(143, 158.6) * mm});
            skLineSegment(sketch, "E21.71.0.1", {"start": v(142, 161.6) * mm, "end": v(142, 158.6) * mm});
            skLineSegment(sketch, "E21.71.0.2", {"start": v(142, 158.6) * mm, "end": v(143, 158.6) * mm});
            skLineSegment(sketch, "E21.71.0.3", {"start": v(142, 161.6) * mm, "end": v(143, 161.6) * mm});
            skLineSegment(sketch, "E21.72.0.0", {"start": v(145, 161.6) * mm, "end": v(145, 158.6) * mm});
            skLineSegment(sketch, "E21.72.0.1", {"start": v(144, 161.6) * mm, "end": v(144, 158.6) * mm});
            skLineSegment(sketch, "E21.72.0.2", {"start": v(144, 158.6) * mm, "end": v(145, 158.6) * mm});
            skLineSegment(sketch, "E21.72.0.3", {"start": v(144, 161.6) * mm, "end": v(145, 161.6) * mm});
            skLineSegment(sketch, "E21.73.0.0", {"start": v(147, 161.6) * mm, "end": v(147, 158.6) * mm});
            skLineSegment(sketch, "E21.73.0.1", {"start": v(146, 161.6) * mm, "end": v(146, 158.6) * mm});
            skLineSegment(sketch, "E21.73.0.2", {"start": v(146, 158.6) * mm, "end": v(147, 158.6) * mm});
            skLineSegment(sketch, "E21.73.0.3", {"start": v(146, 161.6) * mm, "end": v(147, 161.6) * mm});
            skLineSegment(sketch, "E21.74.0.0", {"start": v(149, 161.6) * mm, "end": v(149, 158.6) * mm});
            skLineSegment(sketch, "E21.74.0.1", {"start": v(148, 161.6) * mm, "end": v(148, 158.6) * mm});
            skLineSegment(sketch, "E21.74.0.2", {"start": v(148, 158.6) * mm, "end": v(149, 158.6) * mm});
            skLineSegment(sketch, "E21.74.0.3", {"start": v(148, 161.6) * mm, "end": v(149, 161.6) * mm});
            skLineSegment(sketch, "E21.direction1", {"start": v(0, 158.6) * mm, "end": v(2, 158.6) * mm, "construction": true});
            skLineSegment(sketch, "E22.bottom", {"start": v(0, 158.1) * mm, "end": v(5, 158.1) * mm});
            skLineSegment(sketch, "E22.top", {"start": v(0, 154.1) * mm, "end": v(5, 154.1) * mm});
            skLineSegment(sketch, "E22.left", {"start": v(0, 158.1) * mm, "end": v(0, 154.1) * mm});
            skLineSegment(sketch, "E22.right", {"start": v(5, 158.1) * mm, "end": v(5, 154.1) * mm});
            skLineSegment(sketch, "E23.1.0.0", {"start": v(15, 158.1) * mm, "end": v(15, 154.1) * mm});
            skLineSegment(sketch, "E23.1.0.1", {"start": v(10, 158.1) * mm, "end": v(15, 158.1) * mm});
            skLineSegment(sketch, "E23.1.0.2", {"start": v(10, 158.1) * mm, "end": v(10, 154.1) * mm});
            skLineSegment(sketch, "E23.1.0.3", {"start": v(10, 154.1) * mm, "end": v(15, 154.1) * mm});
            skLineSegment(sketch, "E23.2.0.0", {"start": v(25, 158.1) * mm, "end": v(25, 154.1) * mm});
            skLineSegment(sketch, "E23.2.0.1", {"start": v(20, 158.1) * mm, "end": v(25, 158.1) * mm});
            skLineSegment(sketch, "E23.2.0.2", {"start": v(20, 158.1) * mm, "end": v(20, 154.1) * mm});
            skLineSegment(sketch, "E23.2.0.3", {"start": v(20, 154.1) * mm, "end": v(25, 154.1) * mm});
            skLineSegment(sketch, "E23.3.0.0", {"start": v(35, 158.1) * mm, "end": v(35, 154.1) * mm});
            skLineSegment(sketch, "E23.3.0.1", {"start": v(30, 158.1) * mm, "end": v(35, 158.1) * mm});
            skLineSegment(sketch, "E23.3.0.2", {"start": v(30, 158.1) * mm, "end": v(30, 154.1) * mm});
            skLineSegment(sketch, "E23.3.0.3", {"start": v(30, 154.1) * mm, "end": v(35, 154.1) * mm});
            skLineSegment(sketch, "E23.4.0.0", {"start": v(45, 158.1) * mm, "end": v(45, 154.1) * mm});
            skLineSegment(sketch, "E23.4.0.1", {"start": v(40, 158.1) * mm, "end": v(45, 158.1) * mm});
            skLineSegment(sketch, "E23.4.0.2", {"start": v(40, 158.1) * mm, "end": v(40, 154.1) * mm});
            skLineSegment(sketch, "E23.4.0.3", {"start": v(40, 154.1) * mm, "end": v(45, 154.1) * mm});
            skLineSegment(sketch, "E23.5.0.0", {"start": v(55, 158.1) * mm, "end": v(55, 154.1) * mm});
            skLineSegment(sketch, "E23.5.0.1", {"start": v(50, 158.1) * mm, "end": v(55, 158.1) * mm});
            skLineSegment(sketch, "E23.5.0.2", {"start": v(50, 158.1) * mm, "end": v(50, 154.1) * mm});
            skLineSegment(sketch, "E23.5.0.3", {"start": v(50, 154.1) * mm, "end": v(55, 154.1) * mm});
            skLineSegment(sketch, "E23.6.0.0", {"start": v(65, 158.1) * mm, "end": v(65, 154.1) * mm});
            skLineSegment(sketch, "E23.6.0.1", {"start": v(60, 158.1) * mm, "end": v(65, 158.1) * mm});
            skLineSegment(sketch, "E23.6.0.2", {"start": v(60, 158.1) * mm, "end": v(60, 154.1) * mm});
            skLineSegment(sketch, "E23.6.0.3", {"start": v(60, 154.1) * mm, "end": v(65, 154.1) * mm});
            skLineSegment(sketch, "E23.7.0.0", {"start": v(75, 158.1) * mm, "end": v(75, 154.1) * mm});
            skLineSegment(sketch, "E23.7.0.1", {"start": v(70, 158.1) * mm, "end": v(75, 158.1) * mm});
            skLineSegment(sketch, "E23.7.0.2", {"start": v(70, 158.1) * mm, "end": v(70, 154.1) * mm});
            skLineSegment(sketch, "E23.7.0.3", {"start": v(70, 154.1) * mm, "end": v(75, 154.1) * mm});
            skLineSegment(sketch, "E23.8.0.0", {"start": v(85, 158.1) * mm, "end": v(85, 154.1) * mm});
            skLineSegment(sketch, "E23.8.0.1", {"start": v(80, 158.1) * mm, "end": v(85, 158.1) * mm});
            skLineSegment(sketch, "E23.8.0.2", {"start": v(80, 158.1) * mm, "end": v(80, 154.1) * mm});
            skLineSegment(sketch, "E23.8.0.3", {"start": v(80, 154.1) * mm, "end": v(85, 154.1) * mm});
            skLineSegment(sketch, "E23.9.0.0", {"start": v(95, 158.1) * mm, "end": v(95, 154.1) * mm});
            skLineSegment(sketch, "E23.9.0.1", {"start": v(90, 158.1) * mm, "end": v(95, 158.1) * mm});
            skLineSegment(sketch, "E23.9.0.2", {"start": v(90, 158.1) * mm, "end": v(90, 154.1) * mm});
            skLineSegment(sketch, "E23.9.0.3", {"start": v(90, 154.1) * mm, "end": v(95, 154.1) * mm});
            skLineSegment(sketch, "E23.10.0.0", {"start": v(105, 158.1) * mm, "end": v(105, 154.1) * mm});
            skLineSegment(sketch, "E23.10.0.1", {"start": v(100, 158.1) * mm, "end": v(105, 158.1) * mm});
            skLineSegment(sketch, "E23.10.0.2", {"start": v(100, 158.1) * mm, "end": v(100, 154.1) * mm});
            skLineSegment(sketch, "E23.10.0.3", {"start": v(100, 154.1) * mm, "end": v(105, 154.1) * mm});
            skLineSegment(sketch, "E23.11.0.0", {"start": v(115, 158.1) * mm, "end": v(115, 154.1) * mm});
            skLineSegment(sketch, "E23.11.0.1", {"start": v(110, 158.1) * mm, "end": v(115, 158.1) * mm});
            skLineSegment(sketch, "E23.11.0.2", {"start": v(110, 158.1) * mm, "end": v(110, 154.1) * mm});
            skLineSegment(sketch, "E23.11.0.3", {"start": v(110, 154.1) * mm, "end": v(115, 154.1) * mm});
            skLineSegment(sketch, "E23.12.0.0", {"start": v(125, 158.1) * mm, "end": v(125, 154.1) * mm});
            skLineSegment(sketch, "E23.12.0.1", {"start": v(120, 158.1) * mm, "end": v(125, 158.1) * mm});
            skLineSegment(sketch, "E23.12.0.2", {"start": v(120, 158.1) * mm, "end": v(120, 154.1) * mm});
            skLineSegment(sketch, "E23.12.0.3", {"start": v(120, 154.1) * mm, "end": v(125, 154.1) * mm});
            skLineSegment(sketch, "E23.13.0.0", {"start": v(135, 158.1) * mm, "end": v(135, 154.1) * mm});
            skLineSegment(sketch, "E23.13.0.1", {"start": v(130, 158.1) * mm, "end": v(135, 158.1) * mm});
            skLineSegment(sketch, "E23.13.0.2", {"start": v(130, 158.1) * mm, "end": v(130, 154.1) * mm});
            skLineSegment(sketch, "E23.13.0.3", {"start": v(130, 154.1) * mm, "end": v(135, 154.1) * mm});
            skLineSegment(sketch, "E23.14.0.0", {"start": v(145, 158.1) * mm, "end": v(145, 154.1) * mm});
            skLineSegment(sketch, "E23.14.0.1", {"start": v(140, 158.1) * mm, "end": v(145, 158.1) * mm});
            skLineSegment(sketch, "E23.14.0.2", {"start": v(140, 158.1) * mm, "end": v(140, 154.1) * mm});
            skLineSegment(sketch, "E23.14.0.3", {"start": v(140, 154.1) * mm, "end": v(145, 154.1) * mm});
            skLineSegment(sketch, "E23.direction1", {"start": v(0, 154.1) * mm, "end": v(10, 154.1) * mm, "construction": true});
            skSolve(sketch);
        }
        {
            var Q0;
            Q0 = qSketchRegion(id + "F2", true);
            extrude(context, id + "F3", {"entities" : qUnion([Q0]), "operationType" : NewBodyOperationType.REMOVE, "oppositeDirection" : true, "depth" : 0.5 * mm});
        }
    });
